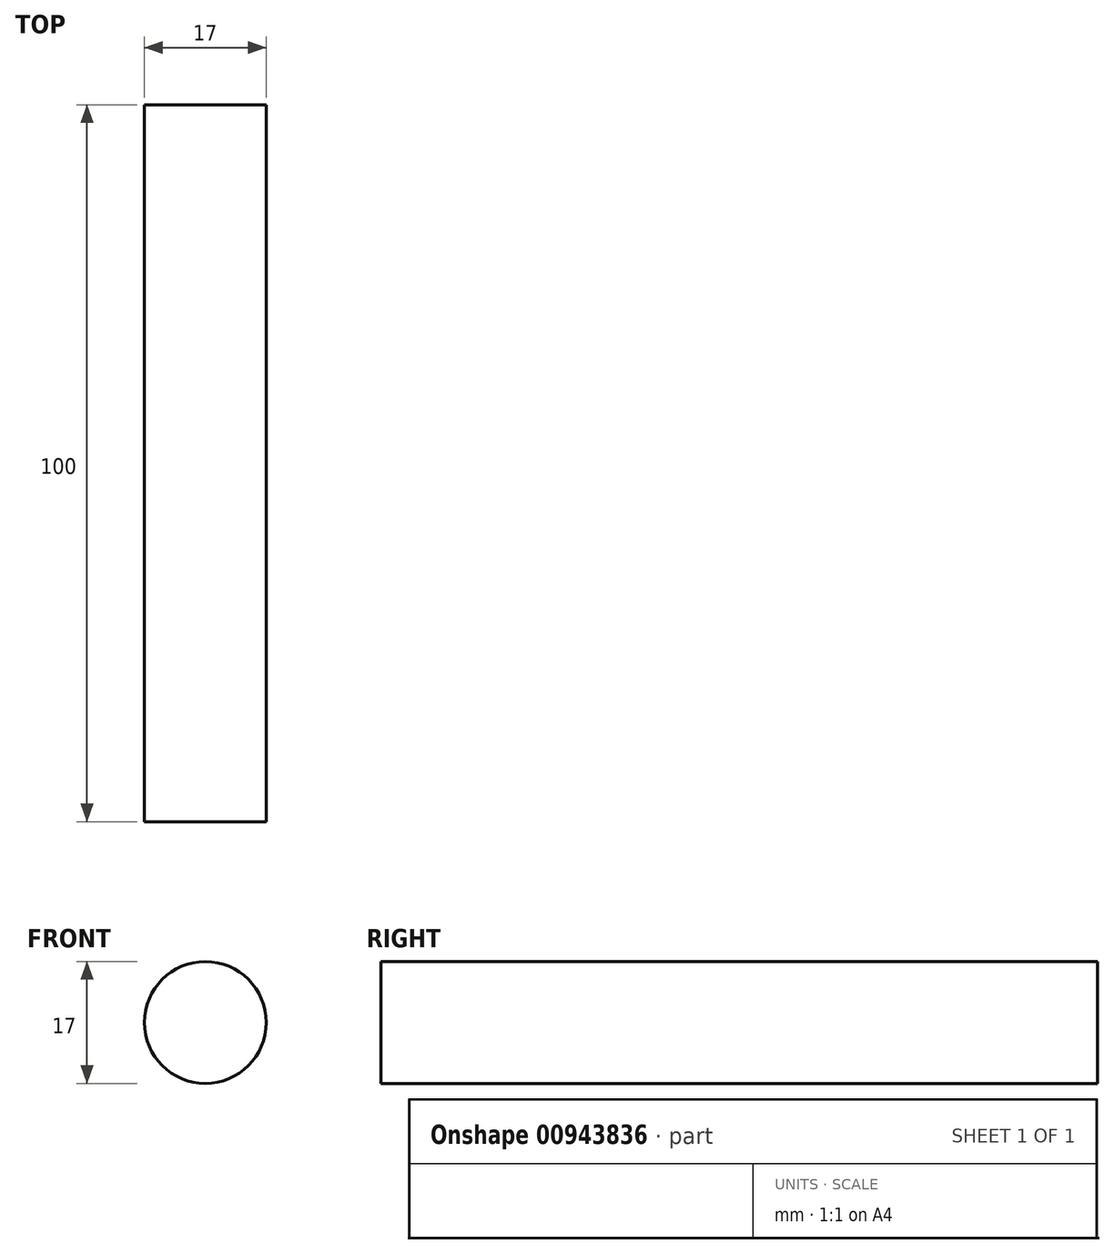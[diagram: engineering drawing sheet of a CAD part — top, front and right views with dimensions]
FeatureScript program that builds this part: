
annotation { "Feature Type Name" : "Feature", "Feature Type Description" : "" }
export const myFeature = defineFeature(function(context is Context, id is Id, definition is map)
    precondition{}
    {
        {
            var Q0;
            Q0=qCreatedBy(makeId("Front.planeOp"),FACE);
            var sketch = newSketch(context, id + "F0", { "sketchPlane" : qUnion([Q0])});
            skCircle(sketch, "E0", {"center": v(0, 0) * mm, "radius": 8.5 * mm});
            skSolve(sketch);
        }
        {
            var Q0;
            Q0 = qSketchRegion(id + "F0", true);
            extrude(context, id + "F1", {"entities" : qUnion([Q0]), "depth" : 100 * mm, "offsetDistance" : 25 * mm, "symmetric" : true});
        }
    });
